# Revit family: Haworth_Tibas_Desk_ReturnExtension_EU_PRELIMINARY
name_source: partatom
category: Furniture
units: mm (PartAtom-declared; Revit-internal decimal feet)

## family parameters
Always vertical = Yes
Cut with Voids When Loaded = No
OmniClass Number = 23.40.70.14.64.11
OmniClass Title = Office Furniture
Room Calculation Point = No
Shared = No
Work Plane-Based = No

## types (6) — shared parameters
Actual Height = 84 cm
Assembly Code = E2020200
Cable Tray Finish = Haworth _ Paint _ Metallic Silver
Description = Haworth - Tibas - Desk - Return Extension
Leg Height = 80 cm
Manufacturer = Haworth
Model = TIREXXXX
Product URL = https://www.haworth.com
Revision Number = 1
Size = Verify Final Dim.w/ Haworth
Trim Finish = Haworth _ Polymer _ Undecided
URL = https://www.haworth.com
Warranty = http://www.haworth.com

## per-type parameters (varying)
| type | Accessory Kit | Actual Depth | Actual Width | Cable Tray Width | Epure Cable Outlet | Extension Width | Flip Top Cable Outlet | Horizontal Cable Tray Single | Horizontal Cable Tray Wire Single | Large | No Accessory Kit | Round Cable Outlet | Small | U Shape Cable Outlet |
| 120 x 80 | Yes | 80 cm | 120 cm | 100 cm | No | 150 cm | No | No | Yes | Yes | No | No | No | Yes |
| 100 x 80 | Yes | 80 cm | 100 cm | 80 cm | No | 130 cm | Yes | No | Yes | Yes | No | No | No | No |
| 80 x 80 | Yes | 80 cm | 80 cm | 60 cm | Yes | 110 cm | No | Yes | No | Yes | No | No | No | No |
| 120 x 60 | Yes | 60 cm | 120 cm | 100 cm | No | 150 cm | No | Yes | No | No | No | Yes | Yes | No |
| 100 x 60 | Yes | 60 cm | 100 cm | 80 cm | Yes | 130 cm | No | Yes | No | No | No | No | Yes | No |
| 80 x 60 | No | 60 cm | 80 cm | 60 cm | No | 110 cm | No | No | No | No | Yes | No | Yes | No |

## geometry (parser evidence)
native form markers: Sweep x37
no freeform markers — native parametric forms only
